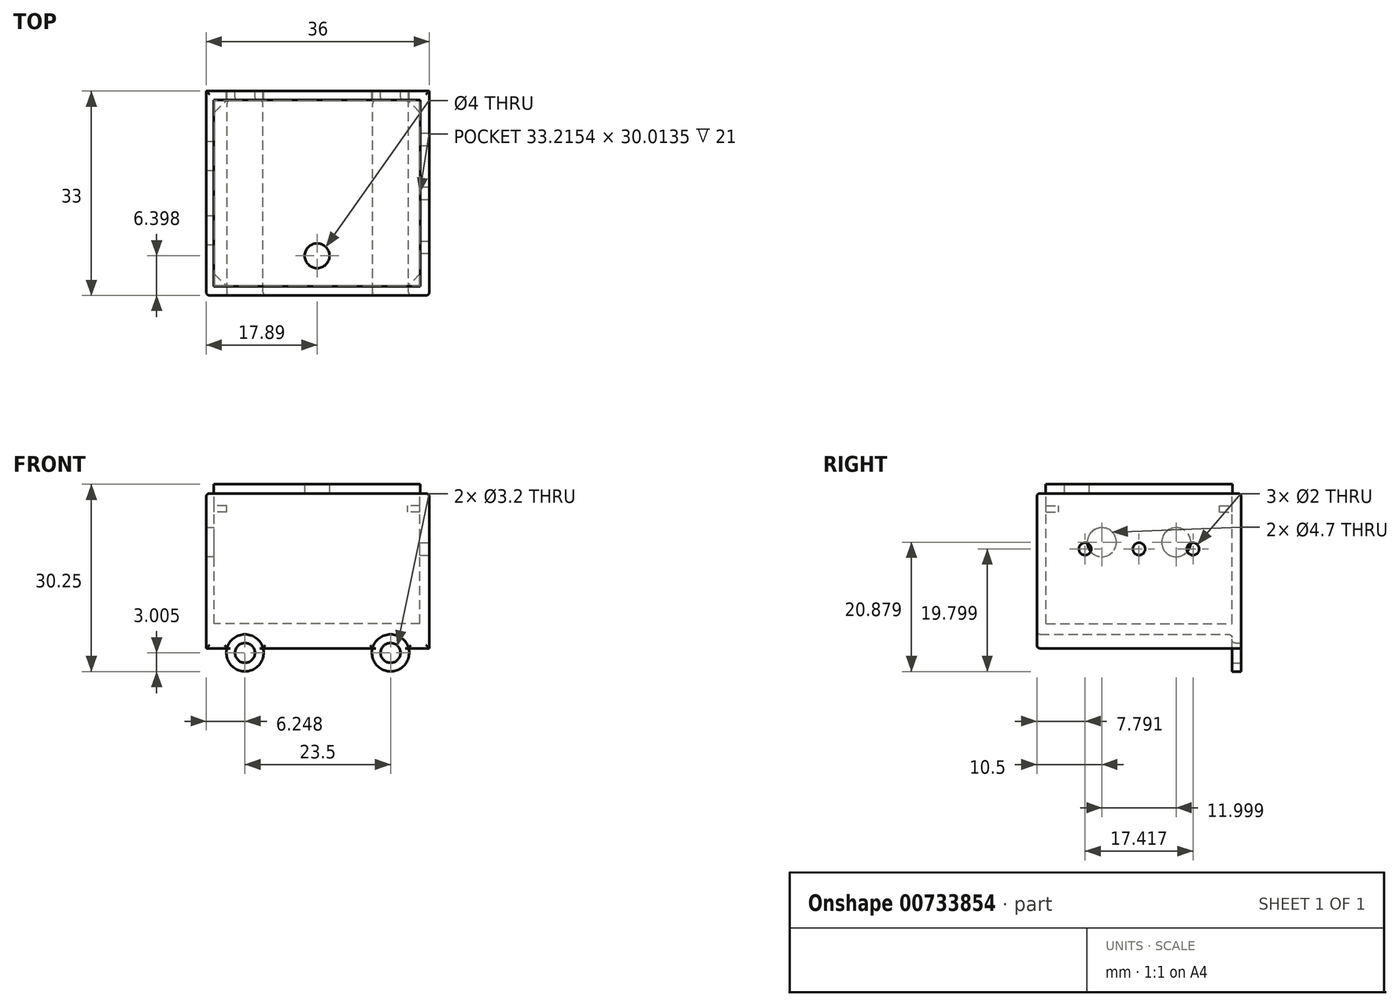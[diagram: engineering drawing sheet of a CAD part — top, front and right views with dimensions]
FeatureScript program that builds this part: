
annotation { "Feature Type Name" : "Feature", "Feature Type Description" : "" }
export const myFeature = defineFeature(function(context is Context, id is Id, definition is map)
    precondition{}
    {
        {
            var Q0;
            Q0=qCreatedBy(makeId("Front.planeOp"),FACE);
            var sketch = newSketch(context, id + "F0", { "sketchPlane" : qUnion([Q0])});
            skLineSegment(sketch, "E0.bottom", {"start": v(-57.26, 57.4) * mm, "end": v(-21.26, 57.4) * mm});
            skLineSegment(sketch, "E0.top", {"start": v(-57.26, 32.4) * mm, "end": v(-53.92, 32.4) * mm});
            skLineSegment(sketch, "E0.left", {"start": v(-57.26, 57.4) * mm, "end": v(-57.26, 32.4) * mm});
            skLineSegment(sketch, "E0.right", {"start": v(-21.26, 57.4) * mm, "end": v(-21.26, 32.4) * mm});
            skLineSegment(sketch, "E1", {"start": v(-69.49, 31.64) * mm, "end": v(14.6, 31.64) * mm, "construction": true});
            skLineSegment(sketch, "E2", {"start": v(-39.26, 58.82) * mm, "end": v(-39.26, 16.7) * mm, "construction": true});
            skPoint(sketch, "E2.startSnap0", {"position": v(-39.26, 57.4) * mm});
            skArc(sketch, "E3", {"start": v(-53.92, 32.4) * mm, "mid": v(-51.01, 28.64) * mm, "end": v(-48.1, 32.4) * mm});
            skArc(sketch, "E4", {"start": v(-30.42, 32.4) * mm, "mid": v(-27.51, 28.64) * mm, "end": v(-24.6, 32.4) * mm});
            skLineSegment(sketch, "E5.trimOffspring", {"start": v(-24.6, 32.4) * mm, "end": v(-21.26, 32.4) * mm});
            skLineSegment(sketch, "E6.trimOffspring", {"start": v(-48.1, 32.4) * mm, "end": v(-30.42, 32.4) * mm});
            skCircle(sketch, "E7", {"center": v(-51.01, 31.64) * mm, "radius": 1.6 * mm});
            skCircle(sketch, "E8", {"center": v(-27.51, 31.64) * mm, "radius": 1.6 * mm});
            skArc(sketch, "E9", {"start": v(-53.92, 32.4) * mm, "mid": v(-51.01, 34.64) * mm, "end": v(-48.1, 32.4) * mm});
            skArc(sketch, "E10", {"start": v(-30.42, 32.4) * mm, "mid": v(-27.51, 34.64) * mm, "end": v(-24.6, 32.4) * mm});
            skSolve(sketch);
        }
        {
            var Q0;
            Q0=makeQuery(id+"F0.imprint","IMPRINT",FACE,{"disambiguationData":[TD([[makeQuery(id+"F0.imprint","IMPRINT",EDGE,{"derivedFrom":sQuery(id+"F0.wireOp",EDGE,"E0.bottom")}),-1.0]])]});
            extrude(context, id + "F1", {"entities" : qUnion([Q0]), "depth" : 33 * mm, "offsetDistance" : 25 * mm});
        }
        {
            var Q0;
            Q0=makeQuery(id+"F0.imprint","IMPRINT",FACE,{"disambiguationData":[TD([[makeQuery(id+"F0.imprint","IMPRINT",EDGE,{"derivedFrom":sQuery(id+"F0.wireOp",EDGE,"E0.bottom")}),-1.0]])]});
            var Q1;
            Q1=makeQuery(id+"F0.imprint","IMPRINT",FACE,{"disambiguationData":[TD([[makeQuery(id+"F0.imprint","IMPRINT",EDGE,{"derivedFrom":sQuery(id+"F0.wireOp",EDGE,"E3")}),1.0]])]});
            var Q2;
            Q2=makeQuery(id+"F0.imprint","IMPRINT",FACE,{"disambiguationData":[TD([[makeQuery(id+"F0.imprint","IMPRINT",EDGE,{"derivedFrom":sQuery(id+"F0.wireOp",EDGE,"E4")}),1.0]])]});
            extrude(context, id + "F2", {"entities" : qUnion([Q0, Q1, Q2]), "operationType" : NewBodyOperationType.ADD, "depth" : 1.5 * mm, "offsetDistance" : 25 * mm});
        }
        {
            var Q0;
            Q0=makeQuery(id+"F1.opExtrude","SWEPT_FACE",FACE,{"disambiguationData":[OSD([sQuery(id+"F0.wireOp",EDGE,"E0.left")])]});
            var sketch = newSketch(context, id + "F3", { "sketchPlane" : qUnion([Q0])});
            skCircle(sketch, "E11", {"center": v(10.5, 49.52) * mm, "radius": 2.35 * mm});
            skCircle(sketch, "E12", {"center": v(22.5, 49.52) * mm, "radius": 2.35 * mm});
            skLineSegment(sketch, "E13", {"start": v(40.31, 49.52) * mm, "end": v(-12.84, 49.52) * mm, "construction": true});
            skLineSegment(sketch, "E14", {"start": v(16.5, 65.41) * mm, "end": v(16.5, 15.04) * mm, "construction": true});
            skPoint(sketch, "E14.startSnap0", {"position": v(16.5, 57.4) * mm});
            skSolve(sketch);
        }
        {
            var Q0;
            Q0 = qSketchRegion(id + "F3", true);
            extrude(context, id + "F4", {"entities" : qUnion([Q0]), "operationType" : NewBodyOperationType.REMOVE, "oppositeDirection" : true, "depth" : 3 * mm, "offsetDistance" : 25 * mm});
        }
        {
            var Q0;
            Q0=makeQuery(id+"F1.opExtrude","SWEPT_FACE",FACE,{"disambiguationData":[OSD([sQuery(id+"F0.wireOp",EDGE,"E0.right")])]});
            var sketch = newSketch(context, id + "F5", { "sketchPlane" : qUnion([Q0])});
            skLineSegment(sketch, "E15", {"start": v(-45.5, 48.44) * mm, "end": v(14.77, 48.44) * mm, "construction": true});
            skLineSegment(sketch, "E16", {"start": v(-16.5, 59.32) * mm, "end": v(-16.5, 10.3) * mm, "construction": true});
            skPoint(sketch, "E16.startSnap0", {"position": v(-16.5, 57.4) * mm});
            skCircle(sketch, "E17", {"center": v(-25.2, 48.44) * mm, "radius": 1 * mm});
            skCircle(sketch, "E18", {"center": v(-7.8, 48.44) * mm, "radius": 1 * mm});
            skCircle(sketch, "E19", {"center": v(-16.5, 48.44) * mm, "radius": 1 * mm});
            skSolve(sketch);
        }
        {
            var Q0;
            Q0=makeQuery(id+"F5.imprint","IMPRINT",FACE,{"disambiguationData":[TD([[makeQuery(id+"F5.imprint","IMPRINT",EDGE,{"derivedFrom":sQuery(id+"F5.wireOp",EDGE,"E18")}),1.0]])]});
            var Q1;
            Q1=makeQuery(id+"F5.imprint","IMPRINT",FACE,{"disambiguationData":[TD([[makeQuery(id+"F5.imprint","IMPRINT",EDGE,{"derivedFrom":sQuery(id+"F5.wireOp",EDGE,"E19")}),1.0]])]});
            var Q2;
            Q2=makeQuery(id+"F5.imprint","IMPRINT",FACE,{"disambiguationData":[TD([[makeQuery(id+"F5.imprint","IMPRINT",EDGE,{"derivedFrom":sQuery(id+"F5.wireOp",EDGE,"E17")}),1.0]])]});
            extrude(context, id + "F6", {"entities" : qUnion([Q0, Q1, Q2]), "operationType" : NewBodyOperationType.REMOVE, "oppositeDirection" : true, "depth" : 3 * mm, "offsetDistance" : 25 * mm});
        }
        {
            var Q0;
            Q0=makeQuery(id+"F1.opExtrude","SWEPT_FACE",FACE,{"disambiguationData":[OSD([sQuery(id+"F0.wireOp",EDGE,"E0.bottom")])]});
            var sketch = newSketch(context, id + "F7", { "sketchPlane" : qUnion([Q0])});
            skLineSegment(sketch, "E20.0", {"start": v(-57.26, -33) * mm, "end": v(-21.26, -33) * mm});
            skLineSegment(sketch, "E21.0", {"start": v(-21.26, -33) * mm, "end": v(-21.26, 0) * mm});
            skLineSegment(sketch, "E22.0", {"start": v(-57.26, 0) * mm, "end": v(-21.26, 0) * mm});
            skLineSegment(sketch, "E23.0", {"start": v(-57.26, -33) * mm, "end": v(-57.26, 0) * mm});
            skLineSegment(sketch, "E24.bottom", {"start": v(-22.76, -31.5) * mm, "end": v(-55.98, -31.5) * mm});
            skLineSegment(sketch, "E24.top", {"start": v(-22.76, -1.49) * mm, "end": v(-55.98, -1.49) * mm});
            skLineSegment(sketch, "E24.left", {"start": v(-22.76, -31.5) * mm, "end": v(-22.76, -1.49) * mm});
            skLineSegment(sketch, "E24.right", {"start": v(-55.98, -31.5) * mm, "end": v(-55.98, -1.49) * mm});
            skLineSegment(sketch, "E25", {"start": v(-22.76, -29.5) * mm, "end": v(-24.76, -31.5) * mm});
            skLineSegment(sketch, "E26", {"start": v(-55.98, -29.5) * mm, "end": v(-53.98, -31.5) * mm});
            skLineSegment(sketch, "E27", {"start": v(-22.76, -3.49) * mm, "end": v(-24.76, -1.49) * mm});
            skLineSegment(sketch, "E28", {"start": v(-55.98, -3.49) * mm, "end": v(-53.98, -1.49) * mm});
            skSolve(sketch);
        }
        {
            var Q0;
            Q0=makeQuery(id+"F7.imprint","IMPRINT",FACE,{"disambiguationData":[TD([[makeQuery(id+"F7.imprint","IMPRINT",EDGE,{"derivedFrom":sQuery(id+"F7.wireOp",EDGE,"E24.bottom")}),-1.0]])]});
            var Q1;
            {var subQ3=sQuery(id+"F7.wireOp",EDGE,"E25");Q1=makeQuery(id+"F7.imprint","IMPRINT",FACE,{"disambiguationData":[TD([[makeQuery(id+"F7.imprint","IMPRINT",EDGE,{"derivedFrom":subQ3}),-1.0]])]});}
            var Q2;
            {var subQ3=sQuery(id+"F7.wireOp",EDGE,"E27");Q2=makeQuery(id+"F7.imprint","IMPRINT",FACE,{"disambiguationData":[TD([[makeQuery(id+"F7.imprint","IMPRINT",EDGE,{"derivedFrom":subQ3}),-1.0]])]});}
            var Q3;
            {var subQ3=sQuery(id+"F7.wireOp",EDGE,"E28");Q3=makeQuery(id+"F7.imprint","IMPRINT",FACE,{"disambiguationData":[TD([[makeQuery(id+"F7.imprint","IMPRINT",EDGE,{"derivedFrom":subQ3}),1.0]])]});}
            extrude(context, id + "F8", {"entities" : qUnion([Q0, Q1, Q2, Q3]), "operationType" : NewBodyOperationType.REMOVE, "oppositeDirection" : true, "depth" : 21 * mm, "offsetDistance" : 25 * mm});
        }
        {
            var Q0;
            Q0=makeQuery(id+"F1.opExtrude","SWEPT_FACE",FACE,{"disambiguationData":[OSD([sQuery(id+"F0.wireOp",EDGE,"E0.bottom")])]});
            var sketch = newSketch(context, id + "F9", { "sketchPlane" : qUnion([Q0])});
            skLineSegment(sketch, "E29.0", {"start": v(-22.76, -31.5) * mm, "end": v(-55.98, -31.5) * mm});
            skLineSegment(sketch, "E30.0", {"start": v(-22.76, -31.5) * mm, "end": v(-22.76, -1.49) * mm});
            skLineSegment(sketch, "E31.0", {"start": v(-22.76, -1.49) * mm, "end": v(-55.98, -1.49) * mm});
            skLineSegment(sketch, "E32.0", {"start": v(-55.98, -31.5) * mm, "end": v(-55.98, -1.49) * mm});
            skLineSegment(sketch, "E33.bottom", {"start": v(-22.7, -31.57) * mm, "end": v(-56.05, -31.57) * mm});
            skLineSegment(sketch, "E33.top", {"start": v(-22.7, -1.42) * mm, "end": v(-56.05, -1.42) * mm});
            skLineSegment(sketch, "E33.left", {"start": v(-22.7, -31.57) * mm, "end": v(-22.7, -1.42) * mm});
            skLineSegment(sketch, "E33.right", {"start": v(-56.05, -31.57) * mm, "end": v(-56.05, -1.42) * mm});
            skCircle(sketch, "E34", {"center": v(-39.37, -26.6) * mm, "radius": 2 * mm});
            skPoint(sketch, "E34.centerSnap0", {"position": v(-39.37, -31.5) * mm});
            skSolve(sketch);
        }
        {
            var Q0;
            Q0 = qSketchRegion(id + "F9", true);
            var Q1;
            Q1=makeQuery(id+"F9.imprint","IMPRINT",FACE,{"disambiguationData":[TD([[makeQuery(id+"F9.imprint","IMPRINT",EDGE,{"derivedFrom":sQuery(id+"F9.wireOp",EDGE,"E29.0")}),-1.0]])]});
            extrude(context, id + "F10", {"entities" : qUnion([Q0, Q1]), "depth" : 1.5 * mm, "offsetDistance" : 25 * mm});
        }
        {
            var Q0;
            {var subQ3=sQuery(id+"F7.wireOp",EDGE,"E25");Q0=makeQuery(id+"F7.imprint","IMPRINT",FACE,{"disambiguationData":[TD([[makeQuery(id+"F7.imprint","IMPRINT",EDGE,{"derivedFrom":subQ3}),1.0]])]});}
            var Q1;
            {var subQ3=sQuery(id+"F7.wireOp",EDGE,"E26");Q1=makeQuery(id+"F7.imprint","IMPRINT",FACE,{"disambiguationData":[TD([[makeQuery(id+"F7.imprint","IMPRINT",EDGE,{"derivedFrom":subQ3}),-1.0]])]});}
            var Q2;
            {var subQ3=sQuery(id+"F7.wireOp",EDGE,"E27");Q2=makeQuery(id+"F7.imprint","IMPRINT",FACE,{"disambiguationData":[TD([[makeQuery(id+"F7.imprint","IMPRINT",EDGE,{"derivedFrom":subQ3}),-1.0]])]});}
            var Q3;
            {var subQ3=sQuery(id+"F7.wireOp",EDGE,"E28");Q3=makeQuery(id+"F7.imprint","IMPRINT",FACE,{"disambiguationData":[TD([[makeQuery(id+"F7.imprint","IMPRINT",EDGE,{"derivedFrom":subQ3}),1.0]])]});}
            extrude(context, id + "F11", {"entities" : qUnion([Q0, Q1, Q2, Q3]), "operationType" : NewBodyOperationType.ADD, "oppositeDirection" : true, "depth" : 3 * mm, "offsetDistance" : 25 * mm, "hasSecondDirection" : true, "secondDirectionOppositeDirection" : true, "secondDirectionDepth" : 2 * mm});
        }
        {
            var Q0;
            Q0=makeQuery(id+"F2.boolean.opBoolean","INTERSECT",EDGE,{"derivedFrom":[makeQuery(id+"F1.opExtrude","SWEPT_FACE",FACE,{"disambiguationData":[OSD([sQuery(id+"F0.wireOp",EDGE,"E9")])]}),makeQuery(id+"F2.opExtrude","CAP_FACE",FACE,{"disambiguationData":[OSD([sQuery(id+"F0.wireOp",EDGE,"E0.bottom"),sQuery(id+"F0.wireOp",EDGE,"E0.top"),sQuery(id+"F0.wireOp",EDGE,"E0.left"),sQuery(id+"F0.wireOp",EDGE,"E0.right"),sQuery(id+"F0.wireOp",EDGE,"E3"),sQuery(id+"F0.wireOp",EDGE,"E4"),sQuery(id+"F0.wireOp",EDGE,"E5.trimOffspring"),sQuery(id+"F0.wireOp",EDGE,"E6.trimOffspring"),sQuery(id+"F0.wireOp",EDGE,"E7"),sQuery(id+"F0.wireOp",EDGE,"E8")])],"isStart":false})]});
            var Q1;
            Q1=makeQuery(id+"F2.opExtrude","CAP_EDGE",EDGE,{"disambiguationData":[OSD([sQuery(id+"F0.wireOp",EDGE,"E8")])],"isStart":false});
            var Q2;
            Q2=makeQuery(id+"F2.opExtrude","CAP_EDGE",EDGE,{"disambiguationData":[OSD([sQuery(id+"F0.wireOp",EDGE,"E7")])],"isStart":false});
            var Q3;
            Q3=makeQuery(id+"F1.opExtrude","CAP_EDGE",EDGE,{"disambiguationData":[OSD([sQuery(id+"F0.wireOp",EDGE,"E9")])],"isStart":false});
            var Q4;
            Q4=makeQuery(id+"F1.opExtrude","CAP_EDGE",EDGE,{"disambiguationData":[OSD([sQuery(id+"F0.wireOp",EDGE,"E10")])],"isStart":false});
            var Q5;
            Q5=makeQuery(id+"F1.opExtrude","CAP_EDGE",EDGE,{"disambiguationData":[OSD([sQuery(id+"F0.wireOp",EDGE,"E6.trimOffspring")])],"isStart":false});
            var Q6;
            Q6=makeQuery(id+"F1.opExtrude","CAP_EDGE",EDGE,{"disambiguationData":[OSD([sQuery(id+"F0.wireOp",EDGE,"E5.trimOffspring")])],"isStart":false});
            var Q7;
            Q7=makeQuery(id+"F1.opExtrude","CAP_EDGE",EDGE,{"disambiguationData":[OSD([sQuery(id+"F0.wireOp",EDGE,"E0.right")])],"isStart":false});
            var Q8;
            Q8=makeQuery(id+"F1.opExtrude","CAP_EDGE",EDGE,{"disambiguationData":[OSD([sQuery(id+"F0.wireOp",EDGE,"E0.top")])],"isStart":false});
            var Q9;
            Q9=makeQuery(id+"F1.opExtrude","CAP_EDGE",EDGE,{"disambiguationData":[OSD([sQuery(id+"F0.wireOp",EDGE,"E0.bottom")])],"isStart":false});
            var Q10;
            Q10=makeQuery(id+"F1.opExtrude","CAP_EDGE",EDGE,{"disambiguationData":[OSD([sQuery(id+"F0.wireOp",EDGE,"E0.left")])],"isStart":false});
            var Q11;
            Q11=makeQuery(id+"F1.opExtrude","SWEPT_EDGE",EDGE,{"disambiguationData":[OSD([sQuery(id+"F0.wireOp",EDGE,"E0.bottom"),sQuery(id+"F0.wireOp",EDGE,"E0.left")])]});
            var Q12;
            Q12=makeQuery(id+"F1.opExtrude","CAP_EDGE",EDGE,{"disambiguationData":[OSD([sQuery(id+"F0.wireOp",EDGE,"E0.bottom")])],"isStart":true});
            var Q13;
            Q13=makeQuery(id+"F1.opExtrude","SWEPT_EDGE",EDGE,{"disambiguationData":[OSD([sQuery(id+"F0.wireOp",EDGE,"E0.bottom"),sQuery(id+"F0.wireOp",EDGE,"E0.right")])]});
            var Q14;
            Q14=makeQuery(id+"F2.boolean.opBoolean","INTERSECT",EDGE,{"derivedFrom":[makeQuery(id+"F1.opExtrude","SWEPT_FACE",FACE,{"disambiguationData":[OSD([sQuery(id+"F0.wireOp",EDGE,"E10")])]}),makeQuery(id+"F2.opExtrude","CAP_FACE",FACE,{"disambiguationData":[OSD([sQuery(id+"F0.wireOp",EDGE,"E0.bottom"),sQuery(id+"F0.wireOp",EDGE,"E0.top"),sQuery(id+"F0.wireOp",EDGE,"E0.left"),sQuery(id+"F0.wireOp",EDGE,"E0.right"),sQuery(id+"F0.wireOp",EDGE,"E3"),sQuery(id+"F0.wireOp",EDGE,"E4"),sQuery(id+"F0.wireOp",EDGE,"E5.trimOffspring"),sQuery(id+"F0.wireOp",EDGE,"E6.trimOffspring"),sQuery(id+"F0.wireOp",EDGE,"E7"),sQuery(id+"F0.wireOp",EDGE,"E8")])],"isStart":false})]});
            fillet(context, id + "F12", {"entities" : qUnion([Q0, Q1, Q2, Q3, Q4, Q5, Q6, Q7, Q8, Q9, Q10, Q11, Q12, Q13, Q14]), "radius" : 0.5 * mm, "tangentPropagation" : true, "allowEdgeOverflow" : false});
        }
    });
